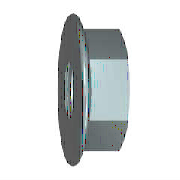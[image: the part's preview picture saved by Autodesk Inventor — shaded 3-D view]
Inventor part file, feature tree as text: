
AUTODESK INVENTOR PART (.ipt)
format: ipt  version: 2023.1 (Build 271208000, 208)  size: 215,040 bytes
history: native  units: mm (DEFAULTED — no unit token found)
features: sketch x3, other x2, chamfer x1, hole x1, plane x1
ambient origin geometry x7: Origin, YZ Plane, XZ Plane, X Axis, Y Axis, Z Axis, Center Point
bodies: Solid1 (feature_tree), Body (feature_tree)
feature tree (8):
  other  "Ring"
  chamfer  "Chamfer1"  Distance=11.8mm
  hole  "Thread"  [1 undecoded]
  other  "Work Axis1"
  plane  "Work Plane1"
  sketch  "Sketch1"  dims[d3=1.0mm d4=11.8mm]
  sketch  "Sketch3"  dims[d8=90.0deg]
  sketch  "Sketch4"  dims[d5=1.0mm d6=9.237604mm d7=5.0mm d9=0.0mm d10=30.0deg d11=8.0mm d24=90.0deg d25=4.134mm d26=6.0mm d27=4.0mm d28=2.0mm d29=14.3117mm d30=8.0mm d31=20.594885mm d12=0.433013mm d13=30.0deg d15=5.0mm d16=30.0deg d45=0.0mm d46=0.433013mm d47=0.0mm d49=0.0mm d51=0.433013mm d52=2.0mm d53=45.0deg d54=0.0mm]
note: 1 required parameter value undecoded (feature->parameter linkage not recoverable at this tier; creation-order binding heuristic only, values carry confidence <= 0.55)
